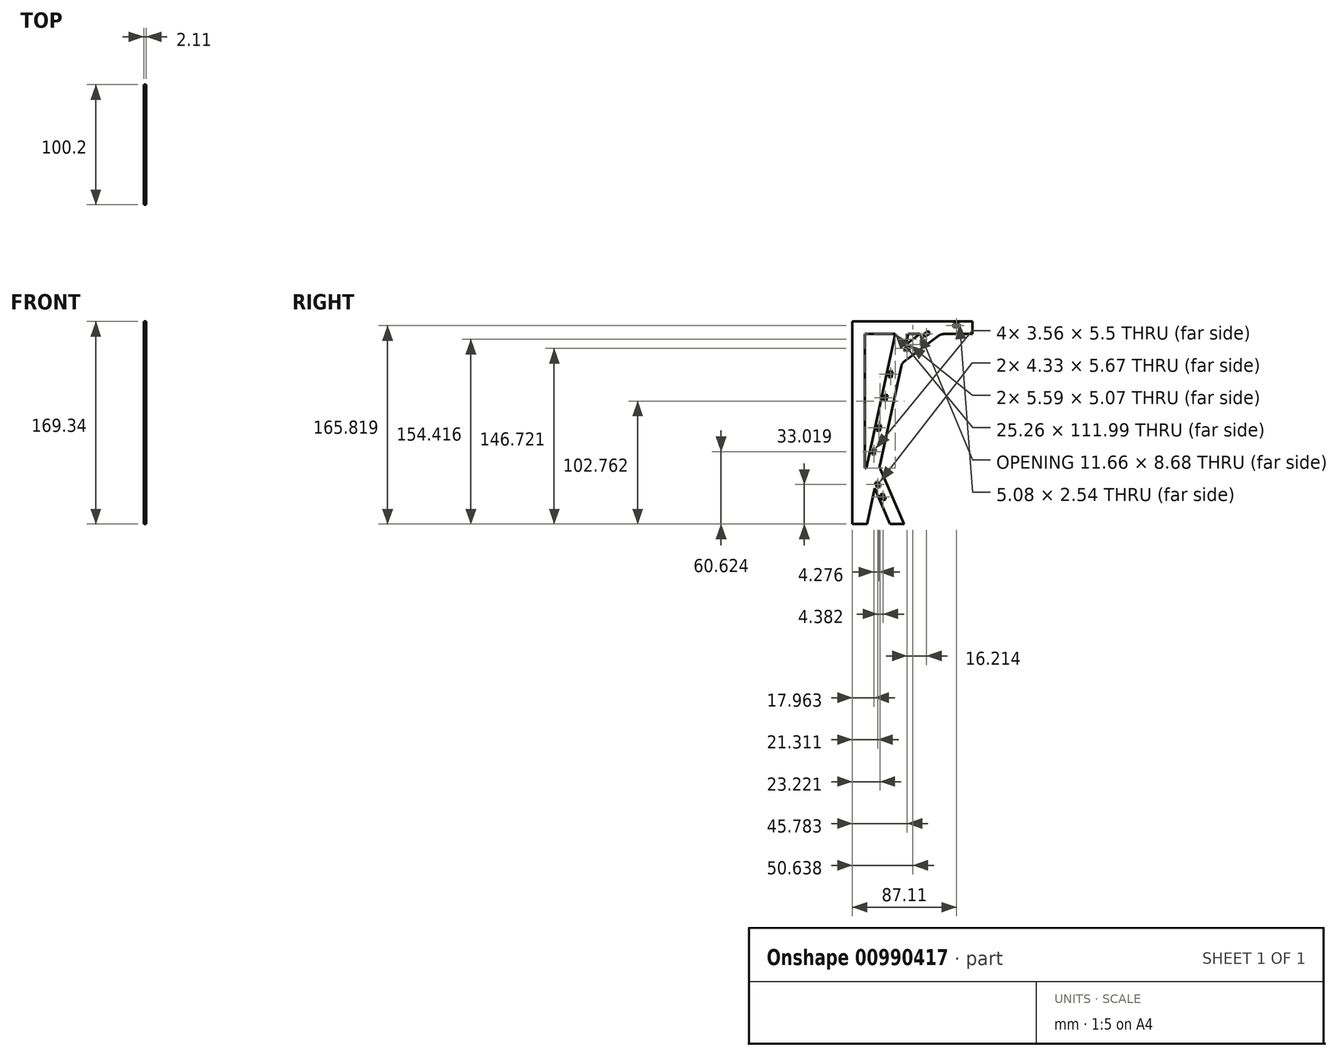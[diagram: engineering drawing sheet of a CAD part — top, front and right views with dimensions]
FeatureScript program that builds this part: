
annotation { "Feature Type Name" : "Feature", "Feature Type Description" : "" }
export const myFeature = defineFeature(function(context is Context, id is Id, definition is map)
    precondition{}
    {
        {
            var Q0;
            Q0=qCreatedBy(makeId("Right.planeOp"),FACE);
            var sketch = newSketch(context, id + "F0", { "sketchPlane" : qUnion([Q0])});
            skLineSegment(sketch, "E0", {"start": v(0, 0) * mm, "end": v(0, 169.34) * mm});
            skLineSegment(sketch, "E1", {"start": v(0, 169.34) * mm, "end": v(200.4, 169.34) * mm});
            skLineSegment(sketch, "E2", {"start": v(0, 0) * mm, "end": v(43.05, 0) * mm, "construction": true});
            skLineSegment(sketch, "E3", {"start": v(43.05, 0) * mm, "end": v(23.47, 45.96) * mm});
            skLineSegment(sketch, "E4", {"start": v(0, 47.82) * mm, "end": v(22.68, 47.82) * mm, "construction": true});
            skLineSegment(sketch, "E5", {"start": v(22.68, 47.82) * mm, "end": v(22.68, 0) * mm, "construction": true});
            skLineSegment(sketch, "E6", {"start": v(23.1, 49.8) * mm, "end": v(40.9, 132) * mm});
            skLineSegment(sketch, "E7", {"start": v(41.4, 134.33) * mm, "end": v(0, 134.33) * mm, "construction": true});
            skLineSegment(sketch, "E8", {"start": v(41.4, 134.33) * mm, "end": v(43.05, 0) * mm, "construction": true});
            skLineSegment(sketch, "E9", {"start": v(43.31, 135.75) * mm, "end": v(72.51, 157.5) * mm});
            skLineSegment(sketch, "E10", {"start": v(74.2, 158.76) * mm, "end": v(74.2, 169.34) * mm, "construction": true});
            skLineSegment(sketch, "E11", {"start": v(74.2, 158.76) * mm, "end": v(0, 158.76) * mm, "construction": true});
            skPoint(sketch, "E12", {"position": v(100.2, 169.34) * mm});
            skLineSegment(sketch, "E13", {"start": v(100.2, 169.34) * mm, "end": v(100.2, 154.3) * mm, "construction": true});
            skLineSegment(sketch, "E14", {"start": v(76.3, 158.76) * mm, "end": v(100.2, 158.76) * mm});
            skLineSegment(sketch, "E15.4", {"start": v(41.18, -0.8) * mm, "end": v(20.56, 47.62) * mm, "construction": true});
            skLineSegment(sketch, "E15.5", {"start": v(20.56, 47.62) * mm, "end": v(39.58, 135.5) * mm});
            skLineSegment(sketch, "E15.6", {"start": v(39.58, 135.5) * mm, "end": v(73.52, 160.79) * mm});
            skLineSegment(sketch, "E15.7", {"start": v(73.52, 160.79) * mm, "end": v(100.2, 160.79) * mm});
            skLineSegment(sketch, "E16.5", {"start": v(11.62, 46.77) * mm, "end": v(31.89, 140.45) * mm});
            skLineSegment(sketch, "E16.6", {"start": v(31.89, 140.45) * mm, "end": v(70.69, 169.35) * mm, "construction": true});
            skLineSegment(sketch, "E16.7", {"start": v(70.69, 169.35) * mm, "end": v(100.2, 169.35) * mm});
            skLineSegment(sketch, "E17", {"start": v(31.89, 140.45) * mm, "end": v(38.14, 169.34) * mm, "construction": true});
            skLineSegment(sketch, "E18", {"start": v(10.6, 158.76) * mm, "end": v(0, 158.76) * mm, "construction": true});
            skLineSegment(sketch, "E19", {"start": v(10.6, 158.76) * mm, "end": v(10.6, 46.77) * mm});
            skLineSegment(sketch, "E20", {"start": v(10.6, 46.77) * mm, "end": v(11.62, 46.77) * mm});
            skLineSegment(sketch, "E21", {"start": v(36.3, 160.79) * mm, "end": v(31.89, 140.45) * mm, "construction": true});
            skLineSegment(sketch, "E22", {"start": v(41.4, 134.33) * mm, "end": v(48.98, 169.34) * mm, "construction": true});
            skLineSegment(sketch, "E23", {"start": v(47.13, 160.79) * mm, "end": v(44.8, 150.07) * mm});
            skLineSegment(sketch, "E24", {"start": v(13.2, 0) * mm, "end": v(0, 0) * mm});
            skLineSegment(sketch, "E25", {"start": v(31.54, 0) * mm, "end": v(43.05, 0) * mm});
            skLineSegment(sketch, "E26", {"start": v(100.2, 158.76) * mm, "end": v(100.2, 169.35) * mm});
            skPoint(sketch, "E27", {"position": v(46.69, 158.76) * mm});
            skPoint(sketch, "E28", {"position": v(56.47, 158.76) * mm});
            skLineSegment(sketch, "E29", {"start": v(46.69, 158.76) * mm, "end": v(56.47, 158.76) * mm});
            skLineSegment(sketch, "E30", {"start": v(44.8, 150.07) * mm, "end": v(46.69, 158.76) * mm});
            skLineSegment(sketch, "E31", {"start": v(10.6, 158.76) * mm, "end": v(35.85, 158.76) * mm});
            skLineSegment(sketch, "E32", {"start": v(35.85, 158.76) * mm, "end": v(31.89, 140.45) * mm});
            skLineSegment(sketch, "E33", {"start": v(44.8, 150.07) * mm, "end": v(56.47, 158.76) * mm});
            skLineSegment(sketch, "E34", {"start": v(30.88, 85.7) * mm, "end": v(20.53, 87.94) * mm, "construction": true});
            skLineSegment(sketch, "E35.0", {"start": v(33.3, -4.15) * mm, "end": v(12.94, 43.67) * mm, "construction": true});
            skLineSegment(sketch, "E36", {"start": v(22.68, 47.82) * mm, "end": v(18.8, 29.9) * mm, "construction": true});
            skLineSegment(sketch, "E37", {"start": v(18.8, 29.9) * mm, "end": v(12.34, 0) * mm});
            skLineSegment(sketch, "E38", {"start": v(18.8, 29.9) * mm, "end": v(31.54, 0) * mm});
            skLineSegment(sketch, "E39", {"start": v(12.34, 0) * mm, "end": v(31.54, 0) * mm});
            skLineSegment(sketch, "E40", {"start": v(20.56, 47.62) * mm, "end": v(40.84, 0) * mm});
            skPoint(sketch, "E41.visualSharp", {"position": v(41.4, 134.33) * mm});
            skArc(sketch, "E41.filletArc", {"start": v(43.31, 135.75) * mm, "mid": v(41.77, 134.1) * mm, "end": v(40.9, 132) * mm});
            skPoint(sketch, "E42.visualSharp", {"position": v(22.68, 47.82) * mm});
            skArc(sketch, "E42.filletArc", {"start": v(23.1, 49.8) * mm, "mid": v(23, 47.85) * mm, "end": v(23.47, 45.96) * mm});
            skPoint(sketch, "E43.visualSharp", {"position": v(74.2, 158.76) * mm});
            skArc(sketch, "E43.filletArc", {"start": v(76.3, 158.76) * mm, "mid": v(74.3, 158.44) * mm, "end": v(72.51, 157.5) * mm});
            skPoint(sketch, "E44", {"position": v(21.75, 93.6) * mm});
            skLineSegment(sketch, "E45", {"start": v(21.75, 93.6) * mm, "end": v(22.1, 95.21) * mm});
            skLineSegment(sketch, "E46", {"start": v(22.1, 95.21) * mm, "end": v(26.54, 94.25) * mm});
            skLineSegment(sketch, "E47", {"start": v(29.56, 96.2) * mm, "end": v(37.5, 132.86) * mm});
            skLineSegment(sketch, "E48", {"start": v(35.55, 135.88) * mm, "end": v(31.1, 136.84) * mm});
            skPoint(sketch, "E49.visualSharp", {"position": v(38.03, 135.35) * mm});
            skArc(sketch, "E49.filletArc", {"start": v(37.5, 132.86) * mm, "mid": v(37.15, 134.78) * mm, "end": v(35.55, 135.88) * mm});
            skPoint(sketch, "E50.visualSharp", {"position": v(29.02, 93.72) * mm});
            skArc(sketch, "E50.filletArc", {"start": v(26.54, 94.25) * mm, "mid": v(28.45, 94.6) * mm, "end": v(29.56, 96.2) * mm});
            skLineSegment(sketch, "E51", {"start": v(21.75, 93.6) * mm, "end": v(32.1, 91.37) * mm, "construction": true});
            skLineSegment(sketch, "E52.0", {"start": v(35.01, 133.4) * mm, "end": v(30.57, 134.36) * mm});
            skLineSegment(sketch, "E52.1", {"start": v(22.64, 97.7) * mm, "end": v(27.08, 96.74) * mm});
            skLineSegment(sketch, "E52.2", {"start": v(27.08, 96.74) * mm, "end": v(27.08, 96.74) * mm});
            skLineSegment(sketch, "E52.3", {"start": v(27.08, 96.74) * mm, "end": v(35.01, 133.4) * mm});
            skLineSegment(sketch, "E52.4", {"start": v(35.01, 133.4) * mm, "end": v(35.01, 133.4) * mm});
            skLineSegment(sketch, "E53.MirrorCS", {"start": v(21.4, 92) * mm, "end": v(25.85, 91.04) * mm});
            skArc(sketch, "E54.MirrorCS", {"start": v(25.85, 91.04) * mm, "mid": v(27.44, 89.94) * mm, "end": v(27.8, 88.02) * mm});
            skLineSegment(sketch, "E55.MirrorCS", {"start": v(27.8, 88.02) * mm, "end": v(19.86, 51.36) * mm});
            skArc(sketch, "E56.MirrorCS", {"start": v(19.86, 51.36) * mm, "mid": v(18.75, 49.76) * mm, "end": v(16.84, 49.41) * mm});
            skLineSegment(sketch, "E57.MirrorCS", {"start": v(16.84, 49.41) * mm, "end": v(12.4, 50.38) * mm});
            skLineSegment(sketch, "E58.MirrorCS", {"start": v(17.37, 51.9) * mm, "end": v(12.94, 52.86) * mm});
            skLineSegment(sketch, "E59.MirrorCS", {"start": v(25.3, 88.56) * mm, "end": v(17.37, 51.9) * mm});
            skLineSegment(sketch, "E60.MirrorCS", {"start": v(20.87, 89.52) * mm, "end": v(25.3, 88.56) * mm});
            skLineSegment(sketch, "E61", {"start": v(33.72, 127.42) * mm, "end": v(31.23, 127.96) * mm});
            skLineSegment(sketch, "E62", {"start": v(31.23, 127.96) * mm, "end": v(30.16, 123) * mm});
            skLineSegment(sketch, "E63", {"start": v(30.16, 123) * mm, "end": v(32.64, 122.46) * mm});
            skLineSegment(sketch, "E64", {"start": v(28.37, 102.7) * mm, "end": v(25.88, 103.24) * mm});
            skLineSegment(sketch, "E65", {"start": v(25.88, 103.24) * mm, "end": v(26.96, 108.2) * mm});
            skLineSegment(sketch, "E66", {"start": v(26.96, 108.2) * mm, "end": v(29.44, 107.66) * mm});
            skLineSegment(sketch, "E67.MirrorCS", {"start": v(24.02, 82.6) * mm, "end": v(21.54, 83.13) * mm});
            skLineSegment(sketch, "E68.MirrorCS", {"start": v(21.54, 83.13) * mm, "end": v(20.46, 78.17) * mm});
            skLineSegment(sketch, "E69.MirrorCS", {"start": v(20.46, 78.17) * mm, "end": v(22.94, 77.63) * mm});
            skLineSegment(sketch, "E70.MirrorCS", {"start": v(17.26, 63.37) * mm, "end": v(19.74, 62.84) * mm});
            skLineSegment(sketch, "E71.MirrorCS", {"start": v(16.19, 58.4) * mm, "end": v(17.26, 63.37) * mm});
            skLineSegment(sketch, "E72.MirrorCS", {"start": v(18.67, 57.87) * mm, "end": v(16.19, 58.4) * mm});
            skLineSegment(sketch, "E73", {"start": v(31.89, 140.45) * mm, "end": v(41.4, 134.33) * mm, "construction": true});
            skLineSegment(sketch, "E74.MirrorCS", {"start": v(37.56, 139.02) * mm, "end": v(34.85, 142.66) * mm});
            skArc(sketch, "E75.MirrorCS", {"start": v(41.12, 138.5) * mm, "mid": v(39.23, 138.02) * mm, "end": v(37.56, 139.02) * mm});
            skLineSegment(sketch, "E76.MirrorCS", {"start": v(71.2, 160.9) * mm, "end": v(41.12, 138.5) * mm});
            skArc(sketch, "E77.MirrorCS", {"start": v(71.72, 164.46) * mm, "mid": v(72.2, 162.57) * mm, "end": v(71.2, 160.9) * mm});
            skLineSegment(sketch, "E78.MirrorCS", {"start": v(69, 168.1) * mm, "end": v(71.72, 164.46) * mm});
            skLineSegment(sketch, "E79.MirrorCS", {"start": v(66.97, 166.58) * mm, "end": v(69.69, 162.94) * mm});
            skLineSegment(sketch, "E80.MirrorCS", {"start": v(69.69, 162.94) * mm, "end": v(39.6, 140.53) * mm});
            skLineSegment(sketch, "E81.MirrorCS", {"start": v(64.8, 159.3) * mm, "end": v(63.28, 161.33) * mm});
            skLineSegment(sketch, "E82.MirrorCS", {"start": v(63.28, 161.33) * mm, "end": v(59.2, 158.3) * mm});
            skLineSegment(sketch, "E83.MirrorCS", {"start": v(59.2, 158.3) * mm, "end": v(60.72, 156.26) * mm});
            skLineSegment(sketch, "E84.MirrorCS", {"start": v(47.06, 149.26) * mm, "end": v(48.58, 147.22) * mm});
            skLineSegment(sketch, "E85.MirrorCS", {"start": v(42.99, 146.22) * mm, "end": v(47.06, 149.26) * mm});
            skLineSegment(sketch, "E86.MirrorCS", {"start": v(44.5, 144.19) * mm, "end": v(42.99, 146.22) * mm});
            skLineSegment(sketch, "E87.MirrorCS", {"start": v(39.6, 140.53) * mm, "end": v(36.89, 144.18) * mm});
            skLineSegment(sketch, "E88", {"start": v(70.69, 169.35) * mm, "end": v(70.69, 164.55) * mm});
            skLineSegment(sketch, "E89", {"start": v(68.15, 162) * mm, "end": v(0, 162) * mm});
            skPoint(sketch, "E90.visualSharp", {"position": v(70.69, 162) * mm});
            skArc(sketch, "E90.filletArc", {"start": v(68.15, 162) * mm, "mid": v(69.94, 162.75) * mm, "end": v(70.69, 164.55) * mm});
            skLineSegment(sketch, "E91.0", {"start": v(68.15, 164.55) * mm, "end": v(0, 164.55) * mm});
            skLineSegment(sketch, "E91.1", {"start": v(68.15, 169.63) * mm, "end": v(68.15, 164.55) * mm});
            skLineSegment(sketch, "E92", {"start": v(55.17, 164.55) * mm, "end": v(55.17, 167.09) * mm});
            skLineSegment(sketch, "E93", {"start": v(55.17, 167.09) * mm, "end": v(50.1, 167.09) * mm});
            skLineSegment(sketch, "E94", {"start": v(50.1, 167.09) * mm, "end": v(50.1, 164.55) * mm});
            skLineSegment(sketch, "E95", {"start": v(10.4, 164.55) * mm, "end": v(10.4, 167.09) * mm});
            skLineSegment(sketch, "E96", {"start": v(10.4, 167.09) * mm, "end": v(5.32, 167.09) * mm});
            skLineSegment(sketch, "E97", {"start": v(5.32, 167.09) * mm, "end": v(5.32, 164.55) * mm});
            skLineSegment(sketch, "E98", {"start": v(22.68, 47.82) * mm, "end": v(11.62, 46.77) * mm, "construction": true});
            skLineSegment(sketch, "E99", {"start": v(15.36, 37.97) * mm, "end": v(19.78, 39.85) * mm});
            skLineSegment(sketch, "E100", {"start": v(23.11, 38.51) * mm, "end": v(37.3, 5.2) * mm});
            skLineSegment(sketch, "E101", {"start": v(35.96, 1.87) * mm, "end": v(31.54, -0.01) * mm});
            skPoint(sketch, "E102.visualSharp", {"position": v(38.3, 2.87) * mm});
            skArc(sketch, "E102.filletArc", {"start": v(35.96, 1.87) * mm, "mid": v(37.32, 3.26) * mm, "end": v(37.3, 5.2) * mm});
            skPoint(sketch, "E103.visualSharp", {"position": v(22.12, 40.85) * mm});
            skArc(sketch, "E103.filletArc", {"start": v(23.11, 38.51) * mm, "mid": v(21.72, 39.87) * mm, "end": v(19.78, 39.85) * mm});
            skLineSegment(sketch, "E104.0", {"start": v(34.97, 4.2) * mm, "end": v(25.52, 0.18) * mm});
            skLineSegment(sketch, "E104.1", {"start": v(20.78, 37.52) * mm, "end": v(34.97, 4.2) * mm});
            skLineSegment(sketch, "E104.2", {"start": v(16.36, 35.63) * mm, "end": v(20.78, 37.52) * mm});
            skLineSegment(sketch, "E105", {"start": v(27.86, 20.9) * mm, "end": v(25.52, 19.9) * mm});
            skLineSegment(sketch, "E106", {"start": v(25.52, 19.9) * mm, "end": v(23.53, 24.57) * mm});
            skLineSegment(sketch, "E107", {"start": v(23.53, 24.57) * mm, "end": v(25.87, 25.57) * mm});
            skLineSegment(sketch, "E108", {"start": v(21.48, 35.85) * mm, "end": v(19.15, 34.86) * mm});
            skLineSegment(sketch, "E109", {"start": v(19.15, 34.86) * mm, "end": v(21.14, 30.18) * mm});
            skLineSegment(sketch, "E110", {"start": v(21.14, 30.18) * mm, "end": v(23.48, 31.18) * mm});
            skLineSegment(sketch, "E111", {"start": v(79.6, 169.35) * mm, "end": v(79.6, 164.55) * mm});
            skLineSegment(sketch, "E112", {"start": v(82.14, 162) * mm, "end": v(100.2, 162) * mm});
            skPoint(sketch, "E113.visualSharp", {"position": v(79.6, 162) * mm});
            skArc(sketch, "E113.filletArc", {"start": v(79.6, 164.55) * mm, "mid": v(80.34, 162.75) * mm, "end": v(82.14, 162) * mm});
            skLineSegment(sketch, "E114.0", {"start": v(82.14, 164.55) * mm, "end": v(100.2, 164.55) * mm});
            skLineSegment(sketch, "E114.1", {"start": v(82.14, 169.35) * mm, "end": v(82.14, 164.55) * mm});
            skLineSegment(sketch, "E115", {"start": v(84.57, 164.55) * mm, "end": v(84.57, 167.09) * mm});
            skPoint(sketch, "E115.endSnap0", {"position": v(68.15, 167.09) * mm});
            skLineSegment(sketch, "E116", {"start": v(84.57, 167.09) * mm, "end": v(89.65, 167.09) * mm});
            skLineSegment(sketch, "E117", {"start": v(89.65, 167.09) * mm, "end": v(89.65, 164.55) * mm});
            skSolve(sketch);
        }
        {
            var Q0;
            Q0=makeQuery(id+"F0.imprint","IMPRINT",FACE,{"disambiguationData":[TD([[makeQuery(id+"F0.imprint","IMPRINT",EDGE,{"derivedFrom":sQuery(id+"F0.wireOp",EDGE,"E15.5")}),1.0]])]});
            var Q1;
            {var subQ0=sQuery(id+"F0.wireOp",EDGE,"E92");Q1=makeQuery(id+"F0.imprint","IMPRINT",FACE,{"disambiguationData":[TD([[makeQuery(id+"F0.imprint","IMPRINT",EDGE,{"derivedFrom":subQ0}),-1.0]])]});}
            var Q2;
            {var subQ10=sQuery(id+"F0.wireOp",EDGE,"E89");Q2=makeQuery(id+"F0.imprint","IMPRINT",FACE,{"disambiguationData":[TD([[makeQuery(id+"F0.imprint","IMPRINT",EDGE,{"derivedFrom":subQ10}),-1.0]])]});}
            var Q3;
            {var subQ0=sQuery(id+"F0.wireOp",EDGE,"E88");var subQ1=makeQuery(id+"F0.imprint","IMPRINT",VERTEX,{"derivedFrom":subQ0});Q3=makeQuery(id+"F0.imprint","IMPRINT",FACE,{"disambiguationData":[TD([[makeQuery(id+"F0.imprint","IMPRINT",EDGE,{"disambiguationData":[TD([[subQ1,1.0]])],"derivedFrom":subQ0}),-1.0]])]});}
            var Q4;
            {var subQ3=sQuery(id+"F0.wireOp",EDGE,"E115");Q4=makeQuery(id+"F0.imprint","IMPRINT",FACE,{"disambiguationData":[TD([[makeQuery(id+"F0.imprint","IMPRINT",EDGE,{"derivedFrom":subQ3}),1.0]])]});}
            var Q5;
            {var subQ4=sQuery(id+"F0.wireOp",EDGE,"E112");Q5=makeQuery(id+"F0.imprint","IMPRINT",FACE,{"disambiguationData":[TD([[makeQuery(id+"F0.imprint","IMPRINT",EDGE,{"derivedFrom":subQ4}),1.0]])]});}
            var Q6;
            {var subQ2=sQuery(id+"F0.wireOp",EDGE,"E3");Q6=makeQuery(id+"F0.imprint","IMPRINT",FACE,{"disambiguationData":[TD([[makeQuery(id+"F0.imprint","IMPRINT",EDGE,{"derivedFrom":subQ2}),1.0]])]});}
            var Q7;
            {var subQ5=sQuery(id+"F0.wireOp",EDGE,"E46");Q7=makeQuery(id+"F0.imprint","IMPRINT",FACE,{"disambiguationData":[TD([[makeQuery(id+"F0.imprint","IMPRINT",EDGE,{"derivedFrom":subQ5}),1.0]])]});}
            var Q8;
            {var subQ3=sQuery(id+"F0.wireOp",EDGE,"E52.0");Q8=makeQuery(id+"F0.imprint","IMPRINT",FACE,{"disambiguationData":[TD([[makeQuery(id+"F0.imprint","IMPRINT",EDGE,{"derivedFrom":subQ3}),1.0]])]});}
            var Q9;
            {var subQ7=sQuery(id+"F0.wireOp",EDGE,"E53.MirrorCS");Q9=makeQuery(id+"F0.imprint","IMPRINT",FACE,{"disambiguationData":[TD([[makeQuery(id+"F0.imprint","IMPRINT",EDGE,{"derivedFrom":subQ7}),-1.0]])]});}
            var Q10;
            {var subQ4=sQuery(id+"F0.wireOp",EDGE,"E58.MirrorCS");Q10=makeQuery(id+"F0.imprint","IMPRINT",FACE,{"disambiguationData":[TD([[makeQuery(id+"F0.imprint","IMPRINT",EDGE,{"derivedFrom":subQ4}),-1.0]])]});}
            var Q11;
            {var subQ0=sQuery(id+"F0.wireOp",EDGE,"E95");Q11=makeQuery(id+"F0.imprint","IMPRINT",FACE,{"disambiguationData":[TD([[makeQuery(id+"F0.imprint","IMPRINT",EDGE,{"derivedFrom":subQ0}),1.0]])]});}
            var Q12;
            {var subQ0=sQuery(id+"F0.wireOp",EDGE,"E92");Q12=makeQuery(id+"F0.imprint","IMPRINT",FACE,{"disambiguationData":[TD([[makeQuery(id+"F0.imprint","IMPRINT",EDGE,{"derivedFrom":subQ0}),1.0]])]});}
            extrude(context, id + "F1", {"entities" : qUnion([Q0, Q1, Q2, Q3, Q4, Q5, Q6, Q7, Q8, Q9, Q10, Q11, Q12]), "depth" : 2.1 * mm, "offsetDistance" : 25.4 * mm});
        }
        {
            var Q0;
            Q0=makeQuery(id+"F1.opExtrude","CAP_EDGE",EDGE,{"disambiguationData":[OSD([sQuery(id+"F0.wireOp",EDGE,"E6")])],"isStart":false});
            fillet(context, id + "F2", {"entities" : qUnion([Q0]), "radius" : 0.76 * mm, "tangentPropagation" : true, "allowEdgeOverflow" : false});
        }
    });
